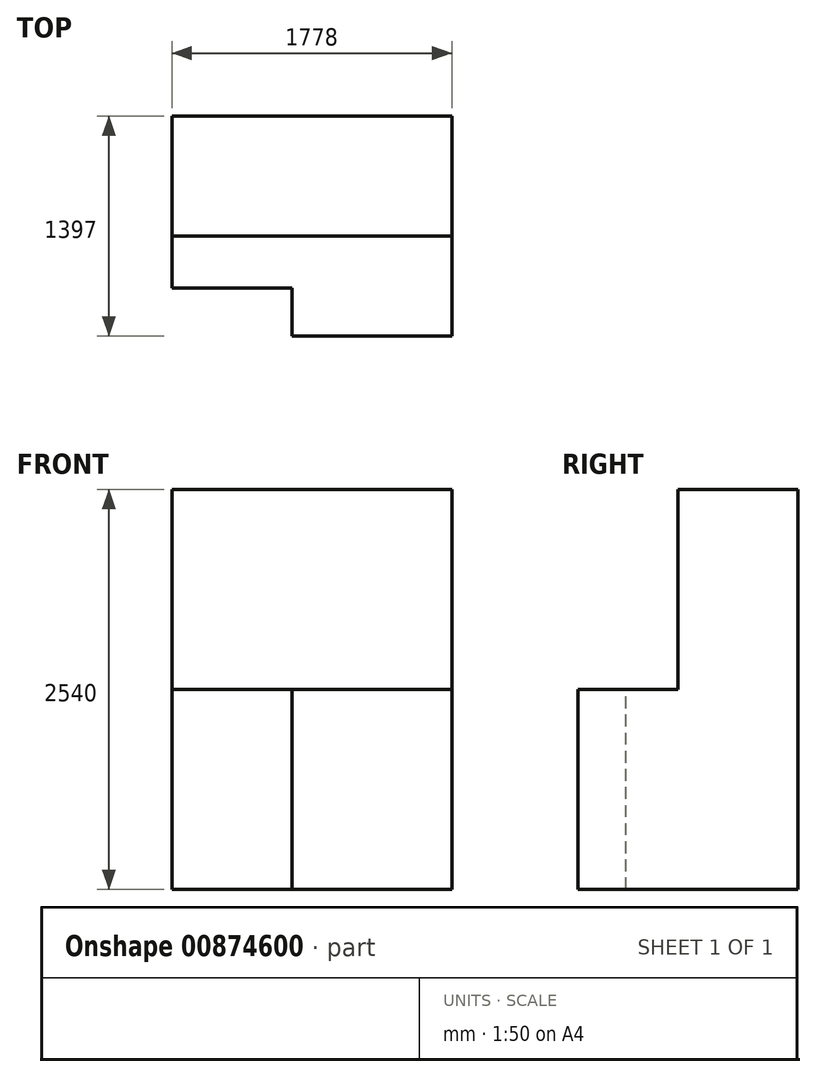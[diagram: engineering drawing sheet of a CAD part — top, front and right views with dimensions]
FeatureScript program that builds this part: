
annotation { "Feature Type Name" : "Feature", "Feature Type Description" : "" }
export const myFeature = defineFeature(function(context is Context, id is Id, definition is map)
    precondition{}
    {
        {
            var Q0;
            Q0=qCreatedBy(makeId("Front.planeOp"),FACE);
            var sketch = newSketch(context, id + "F0", { "sketchPlane" : qUnion([Q0])});
            skLineSegment(sketch, "E0.bottom", {"start": v(0, 0) * mm, "end": v(-1778, 0) * mm});
            skLineSegment(sketch, "E0.top", {"start": v(0, 2540) * mm, "end": v(-1778, 2540) * mm});
            skLineSegment(sketch, "E0.left", {"start": v(0, 0) * mm, "end": v(0, 2540) * mm});
            skLineSegment(sketch, "E0.right", {"start": v(-1778, 0) * mm, "end": v(-1778, 2540) * mm});
            skSolve(sketch);
        }
        {
            var Q0;
            Q0=makeQuery(id+"F0.imprint","IMPRINT",FACE,{"disambiguationData":[TD([[makeQuery(id+"F0.imprint","IMPRINT",EDGE,{"derivedFrom":sQuery(id+"F0.wireOp",EDGE,"E0.bottom")}),-1.0]])]});
            extrude(context, id + "F1", {"entities" : qUnion([Q0]), "depth" : 762 * mm, "offsetDistance" : 25.4 * mm});
        }
        {
            var Q0;
            Q0=makeQuery(id+"F1.opExtrude","CAP_FACE",FACE,{"disambiguationData":[OSD([sQuery(id+"F0.wireOp",EDGE,"E0.bottom"),sQuery(id+"F0.wireOp",EDGE,"E0.top"),sQuery(id+"F0.wireOp",EDGE,"E0.left"),sQuery(id+"F0.wireOp",EDGE,"E0.right")])],"isStart":false});
            var sketch = newSketch(context, id + "F2", { "sketchPlane" : qUnion([Q0])});
            skLineSegment(sketch, "E1.bottom", {"start": v(-1778, 0) * mm, "end": v(0, 0) * mm});
            skLineSegment(sketch, "E1.top", {"start": v(-1778, 1270) * mm, "end": v(0, 1270) * mm});
            skLineSegment(sketch, "E1.left", {"start": v(-1778, 0) * mm, "end": v(-1778, 1270) * mm});
            skLineSegment(sketch, "E1.right", {"start": v(0, 0) * mm, "end": v(0, 1270) * mm});
            skSolve(sketch);
        }
        {
            var Q0;
            Q0=makeQuery(id+"F2.imprint","IMPRINT",FACE,{"disambiguationData":[TD([[makeQuery(id+"F2.imprint","IMPRINT",EDGE,{"derivedFrom":sQuery(id+"F2.wireOp",EDGE,"E1.bottom")}),-1.0]])]});
            var sketch = newSketch(context, id + "F3", { "sketchPlane" : qUnion([Q0])});
            skLineSegment(sketch, "E2.bottom", {"start": v(0, 0) * mm, "end": v(-1016, 0) * mm});
            skLineSegment(sketch, "E2.top", {"start": v(0, 1270) * mm, "end": v(-1016, 1270) * mm});
            skLineSegment(sketch, "E2.left", {"start": v(0, 0) * mm, "end": v(0, 1270) * mm});
            skLineSegment(sketch, "E2.right", {"start": v(-1016, 0) * mm, "end": v(-1016, 1270) * mm});
            skSolve(sketch);
        }
        {
            var Q0;
            Q0=makeQuery(id+"F3.imprint","IMPRINT",FACE,{"disambiguationData":[TD([[makeQuery(id+"F3.imprint","IMPRINT",EDGE,{"derivedFrom":sQuery(id+"F3.wireOp",EDGE,"E2.bottom")}),-1.0]])]});
            extrude(context, id + "F4", {"entities" : qUnion([Q0]), "operationType" : NewBodyOperationType.ADD, "depth" : 635 * mm, "offsetDistance" : 25.4 * mm});
        }
        {
            var Q0;
            Q0=makeQuery(id+"F2.imprint","IMPRINT",FACE,{"disambiguationData":[TD([[makeQuery(id+"F2.imprint","IMPRINT",EDGE,{"derivedFrom":sQuery(id+"F2.wireOp",EDGE,"E1.bottom")}),-1.0]])]});
            extrude(context, id + "F5", {"entities" : qUnion([Q0]), "operationType" : NewBodyOperationType.ADD, "depth" : 330.2 * mm, "offsetDistance" : 25.4 * mm});
        }
    });
